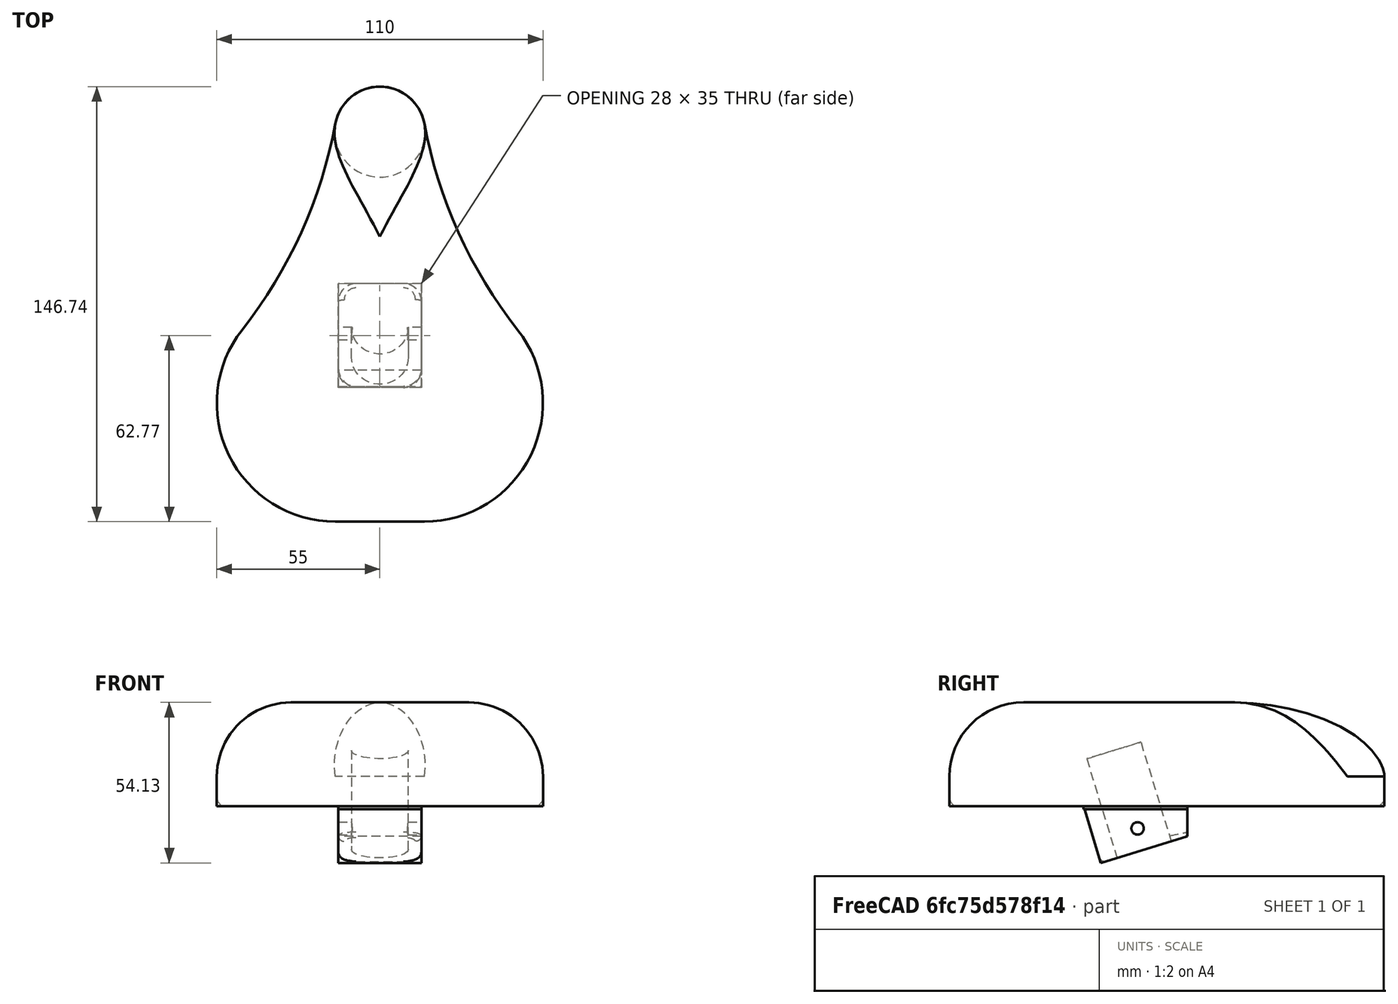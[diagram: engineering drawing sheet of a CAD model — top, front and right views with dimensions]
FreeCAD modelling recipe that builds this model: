
FCSTD DOCUMENT  (FreeCAD 0.16R)
Label: Seat1
License: All rights reserved
LicenseURL: http://en.wikipedia.org/wiki/All_rights_reserved
objects: Sketcher::SketchObject×5, PartDesign::Fillet×5, PartDesign::Pad×3, PartDesign::Pocket×2, Mesh::Feature×1
note: 20 computed .brp shape members not serialized (recipe doc carries the construction recipe); baked Part::Feature solids carry a one-line shape summary decoded from their .brp

FEATURE [Sketcher::SketchObject] Sketch
  sketch-geometry (6):
    g0: ArcOfCircle CenterX=0 CenterY=61.212 CenterZ=0 NormalX=0 NormalY=0 NormalZ=1 Radius=15.2569 StartAngle=0.18377 EndAngle=2.95782
    g1: ArcOfCircle CenterX=-15 CenterY=-30.2722 CenterZ=0 NormalX=0 NormalY=0 NormalZ=1 Radius=40 StartAngle=2.47596 EndAngle=4.71239
    g2: ArcOfCircle CenterX=15 CenterY=-30.2722 CenterZ=0 NormalX=0 NormalY=0 NormalZ=1 Radius=40 StartAngle=4.71239 EndAngle=6.94881
    g3: LineSegment StartX=-15 StartY=-70.2722 StartZ=0 EndX=15 EndY=-70.2722 EndZ=0
    g4: ArcOfCircle CenterX=-172.306 CenterY=93.2385 CenterZ=0 NormalX=0 NormalY=0 NormalZ=1 Radius=160 StartAngle=5.61756 EndAngle=6.09941
    g5: ArcOfCircle CenterX=172.306 CenterY=93.2385 CenterZ=0 NormalX=0 NormalY=0 NormalZ=1 Radius=160 StartAngle=3.32537 EndAngle=3.80722
  constraints (22):
    c: Radius(g2) = 40
    c: Radius(g1) = 40
    c: Horizontal(g3)
    c: Coincident(g3,g2)
    c: Coincident(g1,g3)
    c: Coincident(g5,g0)
    c: Coincident(g4,g0)
    c: Coincident(g2,g5)
    c: Coincident(g1,g4)
    c: Radius(g5) = 160
    c: Radius(g4) = 160
    c: DistanceX(g0) = 15
    c: DistanceX(g0) = -15
    c: Symmetric(g2,g1,g-2)
    c: Symmetric(g2,g1,g-2)
    c: DistanceY(g-1,g0) = 64
    c: Distance(g3) = 30
    c: DistanceX(g1,g-1) = 15
    c: Symmetric(g0,g0,g-2)
    c: Tangent(g5,g0)
    c: Tangent(g2,g5)
    c: Tangent(g3,g1)
FEATURE [PartDesign::Pad] Pad
  Length = 35
  Length2 = 100
  Sketch = -> Sketch
  Type = 0
FEATURE [PartDesign::Fillet] Fillet
  Base = -> Pad [Edge4]
  Radius = 25
FEATURE [Sketcher::SketchObject] Sketch001
  Placement = pos=(0,0,0) rot=(1,0,0;3.14159rad)
  Support = -> Fillet [Face4]
  sketch-geometry (4):
    g0: LineSegment StartX=-14 StartY=25 StartZ=0 EndX=14 EndY=25 EndZ=0
    g1: LineSegment StartX=14 StartY=25 StartZ=0 EndX=14 EndY=-10 EndZ=0
    g2: LineSegment StartX=14 StartY=-10 StartZ=0 EndX=-14 EndY=-10 EndZ=0
    g3: LineSegment StartX=-14 StartY=-10 StartZ=0 EndX=-14 EndY=25 EndZ=0
  constraints (12):
    c: Coincident(g0,g1)
    c: Coincident(g1,g2)
    c: Coincident(g2,g3)
    c: Coincident(g3,g0)
    c: Horizontal(g0)
    c: Horizontal(g2)
    c: Vertical(g1)
    c: Vertical(g3)
    c: Symmetric(g0,g0,g-2)
    c: DistanceY(g-1,g1) = -10
    c: DistanceY(g1,g1) = 35
    c: DistanceX(g0,g0) = 28
FEATURE [PartDesign::Pad] Pad001
  Length = 1
  Length2 = 100
  Sketch = -> Sketch001
  Type = 0
FEATURE [Sketcher::SketchObject] Sketch002
  ExternalGeometry = -> [Pad001]
  Placement = pos=(14,0,0) rot=(0.57735,0.57735,0.57735;2.0944rad)
  Support = -> Pad001 [Face3]
  sketch-geometry (4):
    g0: LineSegment StartX=-25 StartY=0 StartZ=0 EndX=-19.1526 EndY=-19.1261 EndZ=0
    g1: LineSegment StartX=10 StartY=0 StartZ=0 EndX=-25 EndY=0 EndZ=0
    g2: LineSegment StartX=10 StartY=0 StartZ=0 EndX=10 EndY=-10.2133 EndZ=0
    g3: LineSegment StartX=-19.1526 StartY=-19.1261 StartZ=0 EndX=10 EndY=-10.2133 EndZ=0
  constraints (11):
    c: Horizontal(g1)
    c: Coincident(g0,g-6)
    c: Vertical(g2)
    c: Angle(g3) = 0.296706
    c: Coincident(g2,g1)
    c: Coincident(g2,g3)
    c: Coincident(g1,g-5)
    c: Coincident(g3,g0)
    c: Perpendicular(g0,g3)
    c: Distance(g0) = 20
    c: DistanceX(g1,g1) = 35
FEATURE [PartDesign::Pad] Pad002
  Length = 28
  Length2 = 100
  Reversed = true
  Sketch = -> Sketch002
  Type = 0
FEATURE [Sketcher::SketchObject] Sketch004
  ExternalGeometry = -> [Pad002]
  Placement = pos=(0,3.7104,-12.1362) rot=(1,0,0;3.4383rad)
  Support = -> Pad002 [Face25]
  sketch-geometry (1):
    g0: Circle CenterX=0 CenterY=8.66532 CenterZ=0 NormalX=0 NormalY=0 NormalZ=1 Radius=9.55
  constraints (2):
    c: Radius(g0) = 9.55
    c: Symmetric(g-3,g-4,g0)
FEATURE [PartDesign::Pocket] Pocket
  Length = 35
  Sketch = -> Sketch004
  Type = 0
FEATURE [Sketcher::SketchObject] Sketch005
  ExternalGeometry = -> [Pocket]
  Placement = pos=(14,0,0) rot=(0.57735,0.57735,0.57735;2.0944rad)
  Support = -> Pocket [Face20]
  sketch-geometry (1):
    g0: Circle CenterX=-6.76907 CenterY=-7.49739 CenterZ=0 NormalX=0 NormalY=0 NormalZ=1 Radius=2.1
  constraints (3):
    c: Radius(g0) = 2.1
    c: PointOnObject(g0,g-3)
    c: Distance(g0,g-3) = 7.5
FEATURE [PartDesign::Pocket] Pocket001
  Length = 5
  Sketch = -> Sketch005
  Type = 1
FEATURE [PartDesign::Fillet] Fillet001
  Base = -> Pocket001 [Edge45,Edge47,Edge53,Edge48]
  Radius = 6
FEATURE [PartDesign::Fillet] Fillet002
  Base = -> Fillet001 [Edge50]
  Radius = 2
FEATURE [PartDesign::Fillet] Fillet003
  Base = -> Fillet002 [Edge38]
  Radius = 3
FEATURE [PartDesign::Fillet] Fillet004
  Base = -> Fillet003 [Edge38,Edge40]
  Radius = 6
FEATURE [Mesh::Feature] Mesh  label="Fillet004 (Meshed)"
